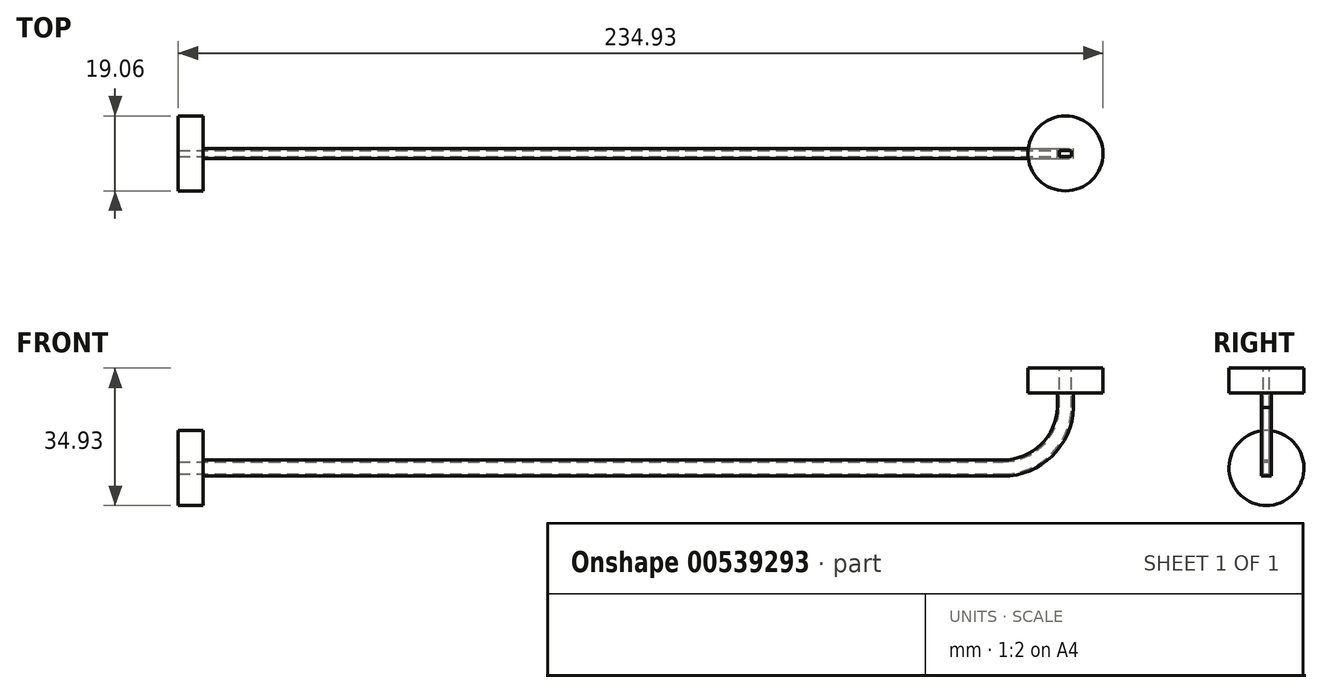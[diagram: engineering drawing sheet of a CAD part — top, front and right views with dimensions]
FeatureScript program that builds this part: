
annotation { "Feature Type Name" : "Feature", "Feature Type Description" : "" }
export const myFeature = defineFeature(function(context is Context, id is Id, definition is map)
    precondition{}
    {
        {
            var Q0;
            Q0=qCreatedBy(makeId("Front.planeOp"),FACE);
            var sketch = newSketch(context, id + "F0", { "sketchPlane" : qUnion([Q0])});
            skLineSegment(sketch, "E0", {"start": v(0, 0) * mm, "end": v(0, -10) * mm});
            skLineSegment(sketch, "E1", {"start": v(-25.4, -25.4) * mm, "end": v(-225.4, -25.4) * mm});
            skLineSegment(sketch, "E2", {"start": v(0, 0) * mm, "end": v(-25.4, 0) * mm});
            skLineSegment(sketch, "E3", {"start": v(-25.4, 0) * mm, "end": v(-25.4, -25.4) * mm});
            skLineSegment(sketch, "E4", {"start": v(-25.4, -25.4) * mm, "end": v(-15.93, -25.4) * mm});
            skArc(sketch, "E5", {"start": v(-15.93, -25.4) * mm, "mid": v(-4.85, -20.92) * mm, "end": v(0, -10) * mm});
            skSolve(sketch);
        }
        {
            var Q0;
            Q0=qCreatedBy(makeId("Top.planeOp"),FACE);
            var sketch = newSketch(context, id + "F1", { "sketchPlane" : qUnion([Q0])});
            skLineSegment(sketch, "E6.bottom", {"start": v(-1.55, -0.78) * mm, "end": v(1.55, -0.78) * mm});
            skLineSegment(sketch, "E6.top", {"start": v(-1.55, 0.77) * mm, "end": v(1.55, 0.77) * mm});
            skLineSegment(sketch, "E6.left", {"start": v(-1.55, -0.78) * mm, "end": v(-1.55, 0.77) * mm});
            skLineSegment(sketch, "E6.right", {"start": v(1.55, -0.78) * mm, "end": v(1.55, 0.77) * mm});
            skPoint(sketch, "E6.middle", {"position": v(0, 0) * mm});
            skLineSegment(sketch, "E7.bottom", {"start": v(-2.05, -1.27) * mm, "end": v(2.05, -1.27) * mm});
            skLineSegment(sketch, "E7.top", {"start": v(-2.05, 1.27) * mm, "end": v(2.05, 1.27) * mm});
            skLineSegment(sketch, "E7.left", {"start": v(-2.05, -1.27) * mm, "end": v(-2.05, 1.27) * mm});
            skLineSegment(sketch, "E7.right", {"start": v(2.05, -1.27) * mm, "end": v(2.05, 1.27) * mm});
            skCircle(sketch, "E8", {"center": v(0, 0) * mm, "radius": 9.53 * mm});
            skSolve(sketch);
        }
        {
            var Q0;
            Q0=qCreatedBy(makeId("Right.planeOp"),FACE);
            cPlane(context, id + "F2", {"entities" : qUnion([Q0]), "cplaneType" : CPlaneType.OFFSET, "offset" : 225.4 * mm, "oppositeDirection" : true, "width" : 150 * mm, "height" : 150 * mm});
        }
        {
            var Q0;
            Q0=qCreatedBy(id+"F2.planeOp",FACE);
            var sketch = newSketch(context, id + "F3", { "sketchPlane" : qUnion([Q0])});
            skLineSegment(sketch, "E9.bottom", {"start": v(-0.78, -26.95) * mm, "end": v(0.78, -26.95) * mm});
            skLineSegment(sketch, "E9.top", {"start": v(-0.78, -23.85) * mm, "end": v(0.77, -23.85) * mm});
            skLineSegment(sketch, "E9.left", {"start": v(-0.78, -26.95) * mm, "end": v(-0.78, -23.85) * mm});
            skLineSegment(sketch, "E9.right", {"start": v(0.78, -26.95) * mm, "end": v(0.77, -23.85) * mm});
            skPoint(sketch, "E9.middle", {"position": v(0, -25.4) * mm});
            skLineSegment(sketch, "E10.bottom", {"start": v(-1.27, -27.45) * mm, "end": v(1.28, -27.45) * mm});
            skLineSegment(sketch, "E10.top", {"start": v(-1.27, -23.35) * mm, "end": v(1.28, -23.35) * mm});
            skLineSegment(sketch, "E10.left", {"start": v(-1.27, -27.45) * mm, "end": v(-1.28, -23.35) * mm});
            skLineSegment(sketch, "E10.right", {"start": v(1.28, -27.45) * mm, "end": v(1.28, -23.35) * mm});
            skCircle(sketch, "E11", {"center": v(0, -25.4) * mm, "radius": 9.53 * mm});
            skSolve(sketch);
        }
        {
            var Q0;
            Q0=makeQuery(id+"F3.imprint","IMPRINT",FACE,{"disambiguationData":[TD([[makeQuery(id+"F3.imprint","IMPRINT",EDGE,{"derivedFrom":sQuery(id+"F3.wireOp",EDGE,"E9.bottom")}),-1.0]])]});
            var Q1;
            Q1=sQuery(id+"F0.wireOp",EDGE,"E1");
            var Q2;
            Q2=sQuery(id+"F0.wireOp",EDGE,"E4");
            var Q3;
            Q3=sQuery(id+"F0.wireOp",EDGE,"E5");
            var Q4;
            Q4=sQuery(id+"F0.wireOp",EDGE,"E0");
            sweep(context, id + "F4", {"profiles" : qUnion([Q0]), "path" : qUnion([Q1, Q2, Q3, Q4])});
        }
        {
            var Q0;
            Q0=makeQuery(id+"F1.imprint","IMPRINT",FACE,{"disambiguationData":[TD([[makeQuery(id+"F1.imprint","IMPRINT",EDGE,{"derivedFrom":sQuery(id+"F1.wireOp",EDGE,"E7.bottom")}),-1.0]])]});
            extrude(context, id + "F5", {"entities" : qUnion([Q0]), "operationType" : NewBodyOperationType.ADD, "oppositeDirection" : true, "depth" : 6.35 * mm, "offsetDistance" : 25 * mm});
        }
        {
            var Q0;
            Q0=makeQuery(id+"F3.imprint","IMPRINT",FACE,{"disambiguationData":[TD([[makeQuery(id+"F3.imprint","IMPRINT",EDGE,{"derivedFrom":sQuery(id+"F3.wireOp",EDGE,"E10.bottom")}),-1.0]])]});
            extrude(context, id + "F6", {"entities" : qUnion([Q0]), "operationType" : NewBodyOperationType.ADD, "depth" : 6.35 * mm, "offsetDistance" : 25 * mm});
        }
    });
